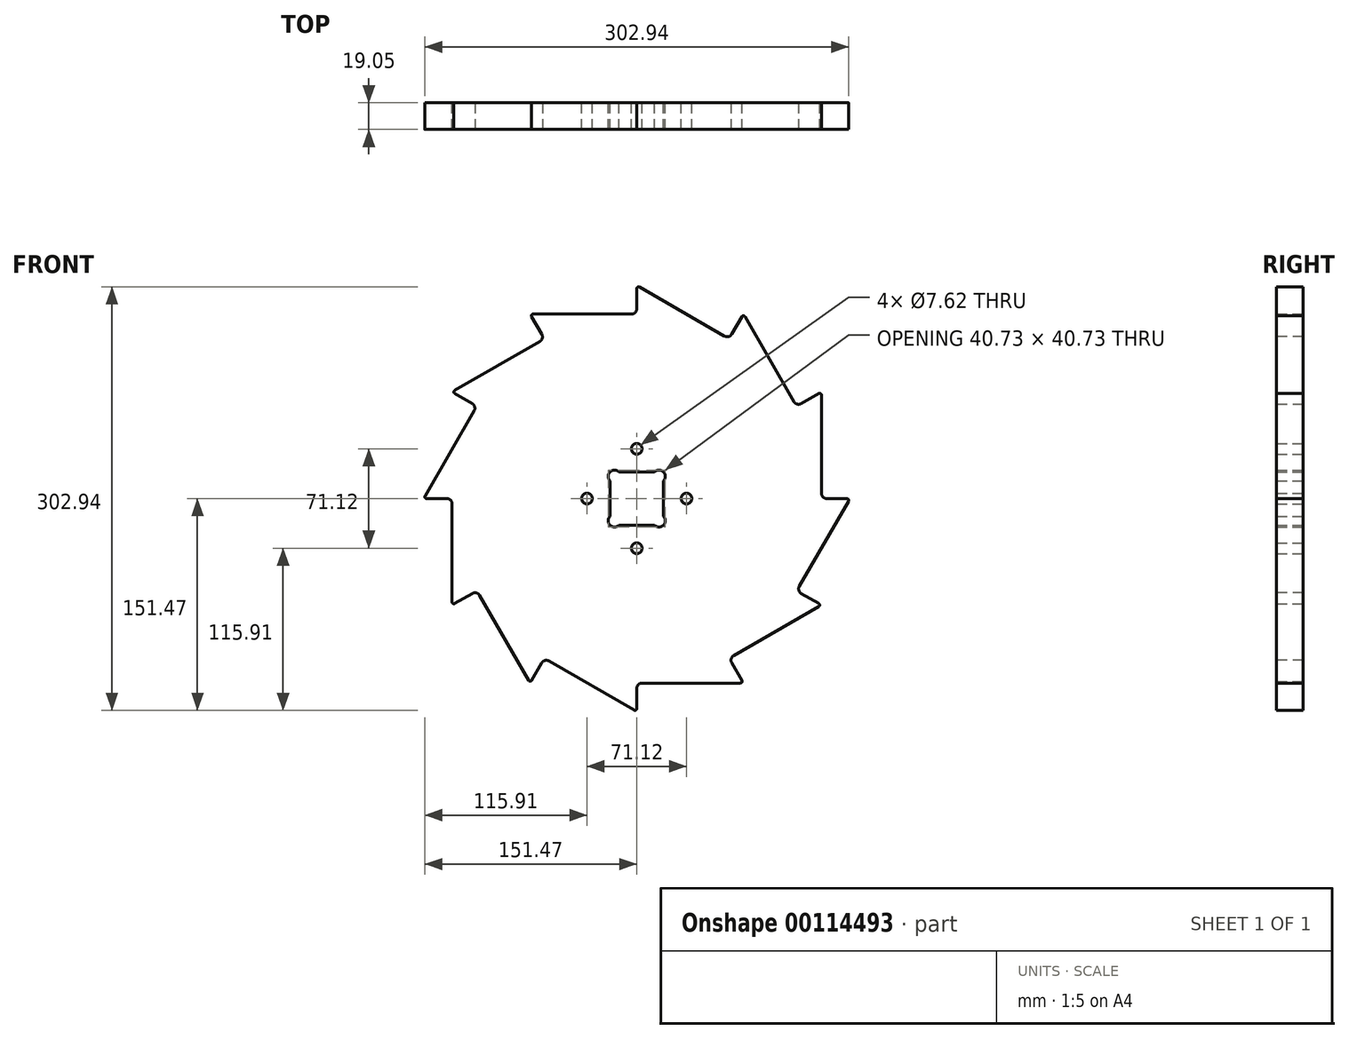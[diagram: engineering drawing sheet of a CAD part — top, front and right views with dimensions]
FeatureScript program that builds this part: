
annotation { "Feature Type Name" : "Feature", "Feature Type Description" : "" }
export const myFeature = defineFeature(function(context is Context, id is Id, definition is map)
    precondition{}
    {
        {
            var Q0;
            Q0=qCreatedBy(makeId("Front.planeOp"),FACE);
            var sketch = newSketch(context, id + "F0", { "sketchPlane" : qUnion([Q0])});
            skCircle(sketch, "E0", {"center": v(0, 0) * mm, "radius": 152.4 * mm, "construction": true});
            skLineSegment(sketch, "E1", {"start": v(0, 0) * mm, "end": v(0, 152.4) * mm, "construction": true});
            skLineSegment(sketch, "E2", {"start": v(0, 0) * mm, "end": v(76.2, 131.98) * mm, "construction": true});
            skLineSegment(sketch, "E3", {"start": v(76.2, 131.98) * mm, "end": v(66, 114.3) * mm});
            skLineSegment(sketch, "E4", {"start": v(66, 114.3) * mm, "end": v(0, 152.4) * mm});
            skLineSegment(sketch, "E5.1.0", {"start": v(0, 131.98) * mm, "end": v(-76.2, 131.98) * mm});
            skLineSegment(sketch, "E5.1.1", {"start": v(0, 152.4) * mm, "end": v(0, 131.98) * mm});
            skLineSegment(sketch, "E5.2.0", {"start": v(-66, 114.3) * mm, "end": v(-131.98, 76.2) * mm});
            skLineSegment(sketch, "E5.2.1", {"start": v(-76.2, 131.98) * mm, "end": v(-66, 114.3) * mm});
            skLineSegment(sketch, "E5.3.0", {"start": v(-114.3, 66) * mm, "end": v(-152.4, 0) * mm});
            skLineSegment(sketch, "E5.3.1", {"start": v(-131.98, 76.2) * mm, "end": v(-114.3, 66) * mm});
            skLineSegment(sketch, "E5.4.0", {"start": v(-131.98, 0) * mm, "end": v(-131.98, -76.2) * mm});
            skLineSegment(sketch, "E5.4.1", {"start": v(-152.4, 0) * mm, "end": v(-131.98, 0) * mm});
            skLineSegment(sketch, "E5.5.0", {"start": v(-114.3, -66) * mm, "end": v(-76.2, -131.98) * mm});
            skLineSegment(sketch, "E5.5.1", {"start": v(-131.98, -76.2) * mm, "end": v(-114.3, -66) * mm});
            skLineSegment(sketch, "E5.6.0", {"start": v(-66, -114.3) * mm, "end": v(0, -152.4) * mm});
            skLineSegment(sketch, "E5.6.1", {"start": v(-76.2, -131.98) * mm, "end": v(-66, -114.3) * mm});
            skLineSegment(sketch, "E5.7.0", {"start": v(0, -131.98) * mm, "end": v(76.2, -131.98) * mm});
            skLineSegment(sketch, "E5.7.1", {"start": v(0, -152.4) * mm, "end": v(0, -131.98) * mm});
            skLineSegment(sketch, "E5.8.0", {"start": v(66, -114.3) * mm, "end": v(131.98, -76.2) * mm});
            skLineSegment(sketch, "E5.8.1", {"start": v(76.2, -131.98) * mm, "end": v(66, -114.3) * mm});
            skLineSegment(sketch, "E5.9.0", {"start": v(114.3, -66) * mm, "end": v(152.4, 0) * mm});
            skLineSegment(sketch, "E5.9.1", {"start": v(131.98, -76.2) * mm, "end": v(114.3, -66) * mm});
            skLineSegment(sketch, "E5.10.0", {"start": v(131.98, 0) * mm, "end": v(131.98, 76.2) * mm});
            skLineSegment(sketch, "E5.10.1", {"start": v(152.4, 0) * mm, "end": v(131.98, 0) * mm});
            skLineSegment(sketch, "E5.11.0", {"start": v(114.3, 66) * mm, "end": v(76.2, 131.98) * mm});
            skLineSegment(sketch, "E5.11.1", {"start": v(131.98, 76.2) * mm, "end": v(114.3, 66) * mm});
            skLineSegment(sketch, "E6.bottom", {"start": v(-6.35, 139.7) * mm, "end": v(-260.35, 139.7) * mm});
            skLineSegment(sketch, "E6.top", {"start": v(-6.35, 228.6) * mm, "end": v(-260.35, 228.6) * mm});
            skLineSegment(sketch, "E6.left", {"start": v(-6.35, 139.7) * mm, "end": v(-6.35, 228.6) * mm});
            skLineSegment(sketch, "E6.right", {"start": v(-260.35, 139.7) * mm, "end": v(-260.35, 228.6) * mm});
            skLineSegment(sketch, "E7", {"start": v(-260.35, 184.15) * mm, "end": v(-215.9, 184.15) * mm, "construction": true});
            skCircle(sketch, "E8", {"center": v(-215.9, 184.15) * mm, "radius": 3.81 * mm});
            skLineSegment(sketch, "E9", {"start": v(0, 0) * mm, "end": v(79.15, 0) * mm, "construction": true});
            skLineSegment(sketch, "E10.bottom", {"start": v(-19.05, -19.05) * mm, "end": v(19.05, -19.05) * mm});
            skLineSegment(sketch, "E10.top", {"start": v(-19.05, 19.05) * mm, "end": v(19.05, 19.05) * mm});
            skLineSegment(sketch, "E10.left", {"start": v(-19.05, -19.05) * mm, "end": v(-19.05, 19.05) * mm});
            skLineSegment(sketch, "E10.right", {"start": v(19.05, -19.05) * mm, "end": v(19.05, 19.05) * mm});
            skLineSegment(sketch, "E11", {"start": v(0, 0) * mm, "end": v(-19.05, 19.05) * mm, "construction": true});
            skCircle(sketch, "E12", {"center": v(-15.88, 15.88) * mm, "radius": 4.5 * mm});
            skPoint(sketch, "E12.first.point", {"position": v(-12.7, 19.05) * mm});
            skPoint(sketch, "E12.second.point", {"position": v(-19.05, 12.7) * mm});
            skCircle(sketch, "E13.MirrorC", {"center": v(15.88, 15.88) * mm, "radius": 4.5 * mm});
            skCircle(sketch, "E14.MirrorC", {"center": v(15.88, -15.88) * mm, "radius": 4.5 * mm});
            skCircle(sketch, "E15.MirrorC", {"center": v(-15.88, -15.88) * mm, "radius": 4.5 * mm});
            skCircle(sketch, "E16", {"center": v(0, 35.56) * mm, "radius": 3.81 * mm});
            skCircle(sketch, "E17", {"center": v(35.56, 0) * mm, "radius": 3.81 * mm});
            skCircle(sketch, "E18", {"center": v(0, -35.56) * mm, "radius": 3.81 * mm});
            skCircle(sketch, "E19", {"center": v(-35.56, 0) * mm, "radius": 3.81 * mm});
            skSolve(sketch);
        }
        {
            var Q0;
            Q0=makeQuery(id+"F0.imprint","IMPRINT",FACE,{"disambiguationData":[TD([[makeQuery(id+"F0.imprint","IMPRINT",EDGE,{"derivedFrom":sQuery(id+"F0.wireOp",EDGE,"E3")}),1.0]])]});
            extrude(context, id + "F1", {"entities" : qUnion([Q0]), "depth" : 19.05 * mm});
        }
        {
            var Q0;
            Q0=makeQuery(id+"F1.opExtrude","SWEPT_EDGE",EDGE,{"disambiguationData":[OSD([sQuery(id+"F0.wireOp",EDGE,"E3"),sQuery(id+"F0.wireOp",EDGE,"E4")])]});
            var Q1;
            Q1=makeQuery(id+"F1.opExtrude","SWEPT_EDGE",EDGE,{"disambiguationData":[OSD([sQuery(id+"F0.wireOp",EDGE,"E5.11.0"),sQuery(id+"F0.wireOp",EDGE,"E5.11.1")])]});
            var Q2;
            Q2=makeQuery(id+"F1.opExtrude","SWEPT_EDGE",EDGE,{"disambiguationData":[OSD([sQuery(id+"F0.wireOp",EDGE,"E5.10.0"),sQuery(id+"F0.wireOp",EDGE,"E5.10.1")])]});
            var Q3;
            Q3=makeQuery(id+"F1.opExtrude","SWEPT_EDGE",EDGE,{"disambiguationData":[OSD([sQuery(id+"F0.wireOp",EDGE,"E5.9.0"),sQuery(id+"F0.wireOp",EDGE,"E5.9.1")])]});
            var Q4;
            Q4=makeQuery(id+"F1.opExtrude","SWEPT_EDGE",EDGE,{"disambiguationData":[OSD([sQuery(id+"F0.wireOp",EDGE,"E5.8.0"),sQuery(id+"F0.wireOp",EDGE,"E5.8.1")])]});
            var Q5;
            Q5=makeQuery(id+"F1.opExtrude","SWEPT_EDGE",EDGE,{"disambiguationData":[OSD([sQuery(id+"F0.wireOp",EDGE,"E5.7.0"),sQuery(id+"F0.wireOp",EDGE,"E5.7.1")])]});
            var Q6;
            Q6=makeQuery(id+"F1.opExtrude","SWEPT_EDGE",EDGE,{"disambiguationData":[OSD([sQuery(id+"F0.wireOp",EDGE,"E5.6.0"),sQuery(id+"F0.wireOp",EDGE,"E5.6.1")])]});
            var Q7;
            Q7=makeQuery(id+"F1.opExtrude","SWEPT_EDGE",EDGE,{"disambiguationData":[OSD([sQuery(id+"F0.wireOp",EDGE,"E5.5.0"),sQuery(id+"F0.wireOp",EDGE,"E5.5.1")])]});
            var Q8;
            Q8=makeQuery(id+"F1.opExtrude","SWEPT_EDGE",EDGE,{"disambiguationData":[OSD([sQuery(id+"F0.wireOp",EDGE,"E5.4.0"),sQuery(id+"F0.wireOp",EDGE,"E5.4.1")])]});
            var Q9;
            Q9=makeQuery(id+"F1.opExtrude","SWEPT_EDGE",EDGE,{"disambiguationData":[OSD([sQuery(id+"F0.wireOp",EDGE,"E5.3.0"),sQuery(id+"F0.wireOp",EDGE,"E5.3.1")])]});
            var Q10;
            Q10=makeQuery(id+"F1.opExtrude","SWEPT_EDGE",EDGE,{"disambiguationData":[OSD([sQuery(id+"F0.wireOp",EDGE,"E5.2.0"),sQuery(id+"F0.wireOp",EDGE,"E5.2.1")])]});
            var Q11;
            Q11=makeQuery(id+"F1.opExtrude","SWEPT_EDGE",EDGE,{"disambiguationData":[OSD([sQuery(id+"F0.wireOp",EDGE,"E5.1.0"),sQuery(id+"F0.wireOp",EDGE,"E5.1.1")])]});
            fillet(context, id + "F2", {"entities" : qUnion([Q0, Q1, Q2, Q3, Q4, Q5, Q6, Q7, Q8, Q9, Q10, Q11]), "radius" : 3.8 * mm, "tangentPropagation" : true, "allowEdgeOverflow" : false});
        }
        {
            var Q0;
            Q0=makeQuery(id+"F1.opExtrude","SWEPT_EDGE",EDGE,{"disambiguationData":[OSD([sQuery(id+"F0.wireOp",EDGE,"E4"),sQuery(id+"F0.wireOp",EDGE,"E5.1.1")])]});
            var Q1;
            Q1=makeQuery(id+"F1.opExtrude","SWEPT_EDGE",EDGE,{"disambiguationData":[OSD([sQuery(id+"F0.wireOp",EDGE,"E3"),sQuery(id+"F0.wireOp",EDGE,"E5.11.0")])]});
            var Q2;
            Q2=makeQuery(id+"F1.opExtrude","SWEPT_EDGE",EDGE,{"disambiguationData":[OSD([sQuery(id+"F0.wireOp",EDGE,"E5.10.0"),sQuery(id+"F0.wireOp",EDGE,"E5.11.1")])]});
            var Q3;
            Q3=makeQuery(id+"F1.opExtrude","SWEPT_EDGE",EDGE,{"disambiguationData":[OSD([sQuery(id+"F0.wireOp",EDGE,"E5.9.0"),sQuery(id+"F0.wireOp",EDGE,"E5.10.1")])]});
            var Q4;
            Q4=makeQuery(id+"F1.opExtrude","SWEPT_EDGE",EDGE,{"disambiguationData":[OSD([sQuery(id+"F0.wireOp",EDGE,"E5.8.0"),sQuery(id+"F0.wireOp",EDGE,"E5.9.1")])]});
            var Q5;
            Q5=makeQuery(id+"F1.opExtrude","SWEPT_EDGE",EDGE,{"disambiguationData":[OSD([sQuery(id+"F0.wireOp",EDGE,"E5.7.0"),sQuery(id+"F0.wireOp",EDGE,"E5.8.1")])]});
            var Q6;
            Q6=makeQuery(id+"F1.opExtrude","SWEPT_EDGE",EDGE,{"disambiguationData":[OSD([sQuery(id+"F0.wireOp",EDGE,"E5.6.0"),sQuery(id+"F0.wireOp",EDGE,"E5.7.1")])]});
            var Q7;
            Q7=makeQuery(id+"F1.opExtrude","SWEPT_EDGE",EDGE,{"disambiguationData":[OSD([sQuery(id+"F0.wireOp",EDGE,"E5.5.0"),sQuery(id+"F0.wireOp",EDGE,"E5.6.1")])]});
            var Q8;
            Q8=makeQuery(id+"F1.opExtrude","SWEPT_EDGE",EDGE,{"disambiguationData":[OSD([sQuery(id+"F0.wireOp",EDGE,"E5.4.0"),sQuery(id+"F0.wireOp",EDGE,"E5.5.1")])]});
            var Q9;
            Q9=makeQuery(id+"F1.opExtrude","SWEPT_EDGE",EDGE,{"disambiguationData":[OSD([sQuery(id+"F0.wireOp",EDGE,"E5.3.0"),sQuery(id+"F0.wireOp",EDGE,"E5.4.1")])]});
            var Q10;
            Q10=makeQuery(id+"F1.opExtrude","SWEPT_EDGE",EDGE,{"disambiguationData":[OSD([sQuery(id+"F0.wireOp",EDGE,"E5.2.0"),sQuery(id+"F0.wireOp",EDGE,"E5.3.1")])]});
            var Q11;
            Q11=makeQuery(id+"F1.opExtrude","SWEPT_EDGE",EDGE,{"disambiguationData":[OSD([sQuery(id+"F0.wireOp",EDGE,"E5.1.0"),sQuery(id+"F0.wireOp",EDGE,"E5.2.1")])]});
            fillet(context, id + "F3", {"entities" : qUnion([Q0, Q1, Q2, Q3, Q4, Q5, Q6, Q7, Q8, Q9, Q10, Q11]), "radius" : 1.27 * mm, "tangentPropagation" : true, "allowEdgeOverflow" : false});
        }
    });
